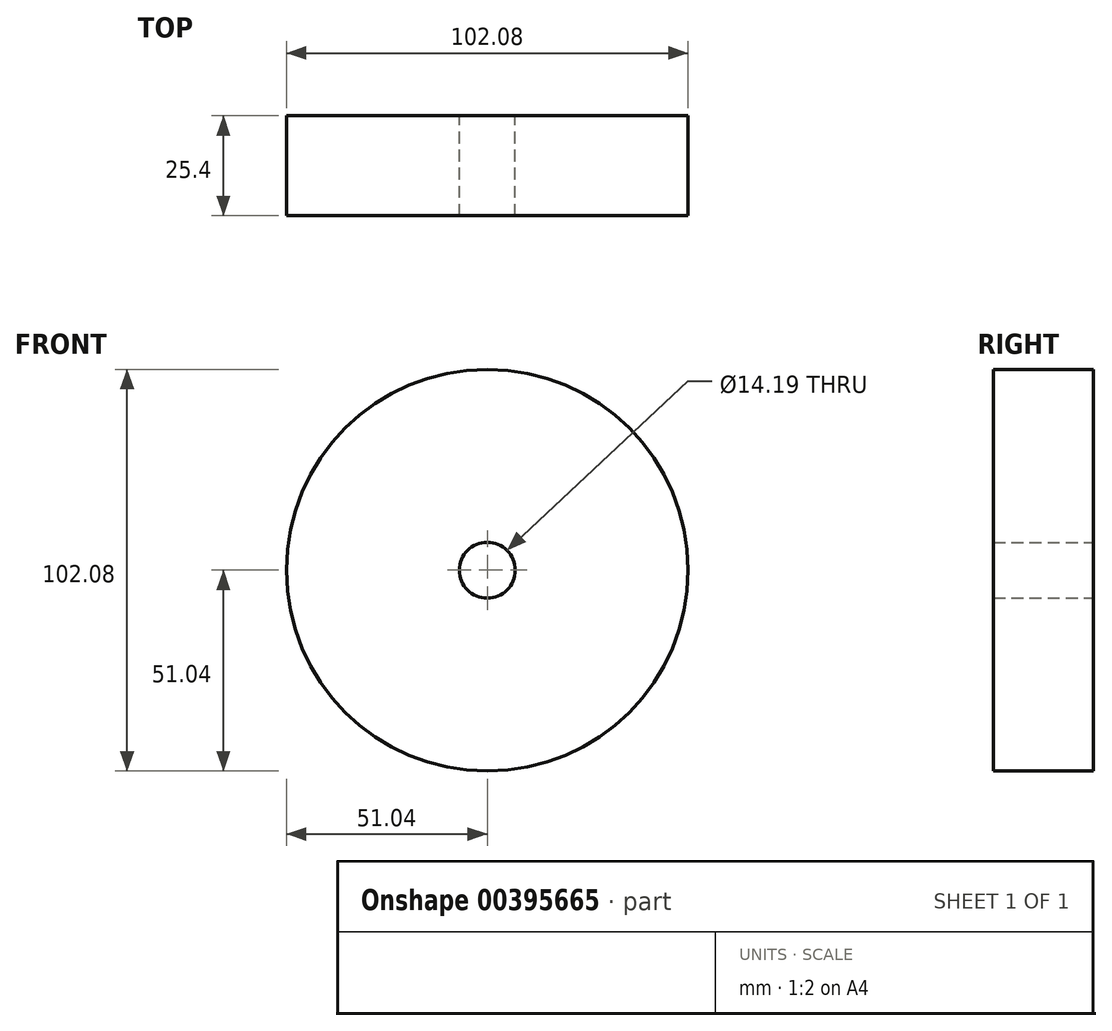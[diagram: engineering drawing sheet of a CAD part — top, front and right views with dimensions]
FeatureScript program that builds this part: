
annotation { "Feature Type Name" : "Feature", "Feature Type Description" : "" }
export const myFeature = defineFeature(function(context is Context, id is Id, definition is map)
    precondition{}
    {
        {
            var Q0;
            Q0=qCreatedBy(makeId("Front.planeOp"),FACE);
            var sketch = newSketch(context, id + "F0", { "sketchPlane" : qUnion([Q0])});
            skCircle(sketch, "E0", {"center": v(0, 0) * mm, "radius": 51.04 * mm});
            skCircle(sketch, "E1", {"center": v(0, 0) * mm, "radius": 7.1 * mm});
            skSolve(sketch);
        }
        {
            var Q0;
            Q0=makeQuery(id+"F0.imprint","IMPRINT",FACE,{"disambiguationData":[TD([[makeQuery(id+"F0.imprint","IMPRINT",EDGE,{"derivedFrom":sQuery(id+"F0.wireOp",EDGE,"E0")}),1.0]])]});
            var Q1;
            Q1 = qSketchRegion(id + "F0", true);
            extrude(context, id + "F1", {"entities" : qUnion([Q0, Q1]), "depth" : 25.4 * mm});
        }
    });
